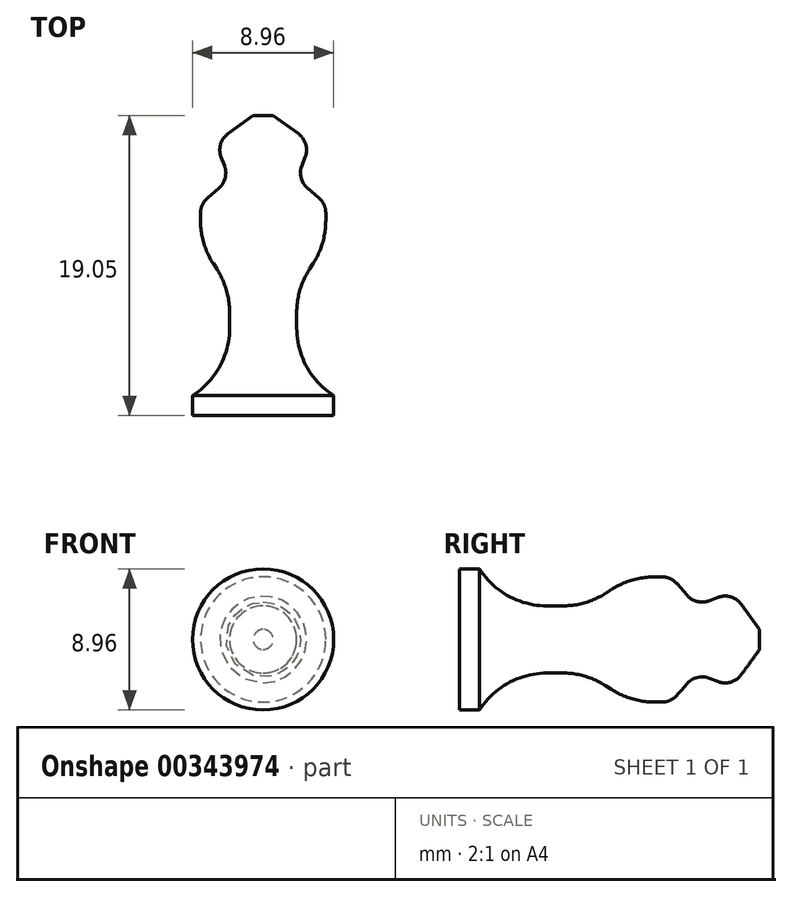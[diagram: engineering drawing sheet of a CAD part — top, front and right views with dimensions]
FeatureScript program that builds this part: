
annotation { "Feature Type Name" : "Feature", "Feature Type Description" : "" }
export const myFeature = defineFeature(function(context is Context, id is Id, definition is map)
    precondition{}
    {
        {
            var Q0;
            Q0=qCreatedBy(makeId("Right.planeOp"),FACE);
            var sketch = newSketch(context, id + "F0", { "sketchPlane" : qUnion([Q0])});
            skLineSegment(sketch, "E0", {"start": v(0, 0) * mm, "end": v(-19.05, 0) * mm});
            skLineSegment(sketch, "E1", {"start": v(-19.05, 0) * mm, "end": v(-19.05, 4.48) * mm});
            skLineSegment(sketch, "E2", {"start": v(-19.05, 4.48) * mm, "end": v(-17.78, 4.48) * mm});
            skLineSegment(sketch, "E3", {"start": v(-17.78, 4.48) * mm, "end": v(-17.46, 2.13) * mm});
            skLineSegment(sketch, "E4", {"start": v(-17.46, 2.13) * mm, "end": v(-11.02, 2.13) * mm});
            skLineSegment(sketch, "E5", {"start": v(-11.02, 2.13) * mm, "end": v(-8.16, 3.98) * mm});
            skLineSegment(sketch, "E6", {"start": v(-8.16, 3.98) * mm, "end": v(-5.61, 3.98) * mm});
            skLineSegment(sketch, "E7", {"start": v(-5.61, 3.98) * mm, "end": v(-4.03, 2.13) * mm});
            skLineSegment(sketch, "E8", {"start": v(-4.03, 2.13) * mm, "end": v(-1.73, 3.03) * mm});
            skLineSegment(sketch, "E9", {"start": v(0, 0.63) * mm, "end": v(-1.73, 3.03) * mm});
            skLineSegment(sketch, "E10", {"start": v(0, 0.64) * mm, "end": v(0, 0) * mm});
            skSolve(sketch);
        }
        {
            var Q0;
            Q0=makeQuery(id+"F0.imprint","IMPRINT",FACE,{"disambiguationData":[TD([[makeQuery(id+"F0.imprint","IMPRINT",EDGE,{"derivedFrom":sQuery(id+"F0.wireOp",EDGE,"E0")}),-1.0]])]});
            var Q1;
            Q1=sQuery(id+"F0.wireOp",EDGE,"E0");
            revolve(context, id + "F1", {"entities" : qUnion([Q0]), "axis" : qUnion([Q1]), "revolveType" : RevolveType.FULL});
        }
        {
            var Q0;
            Q0=makeQuery(id+"F1.opRevolve","SWEPT_EDGE",EDGE,{"disambiguationData":[OSD([sQuery(id+"F0.wireOp",EDGE,"E4"),sQuery(id+"F0.wireOp",EDGE,"E5")])]});
            var Q1;
            Q1=makeQuery(id+"F1.opRevolve","SWEPT_EDGE",EDGE,{"disambiguationData":[OSD([sQuery(id+"F0.wireOp",EDGE,"E5"),sQuery(id+"F0.wireOp",EDGE,"E6")])]});
            var Q2;
            Q2=makeQuery(id+"F1.opRevolve","SWEPT_EDGE",EDGE,{"disambiguationData":[OSD([sQuery(id+"F0.wireOp",EDGE,"E3"),sQuery(id+"F0.wireOp",EDGE,"E4")])]});
            fillet(context, id + "F2", {"entities" : qUnion([Q0, Q1, Q2]), "radius" : 5.08 * mm, "allowEdgeOverflow" : false});
        }
        {
            var Q0;
            Q0=makeQuery(id+"F1.opRevolve","SWEPT_EDGE",EDGE,{"disambiguationData":[OSD([sQuery(id+"F0.wireOp",EDGE,"E6"),sQuery(id+"F0.wireOp",EDGE,"E7")])]});
            var Q1;
            Q1=makeQuery(id+"F1.opRevolve","SWEPT_EDGE",EDGE,{"disambiguationData":[OSD([sQuery(id+"F0.wireOp",EDGE,"E7"),sQuery(id+"F0.wireOp",EDGE,"E8")])]});
            var Q2;
            Q2=makeQuery(id+"F1.opRevolve","SWEPT_EDGE",EDGE,{"disambiguationData":[OSD([sQuery(id+"F0.wireOp",EDGE,"E8"),sQuery(id+"F0.wireOp",EDGE,"E9")])]});
            fillet(context, id + "F3", {"entities" : qUnion([Q0, Q1, Q2]), "radius" : 1.27 * mm, "tangentPropagation" : true, "allowEdgeOverflow" : false});
        }
    });
